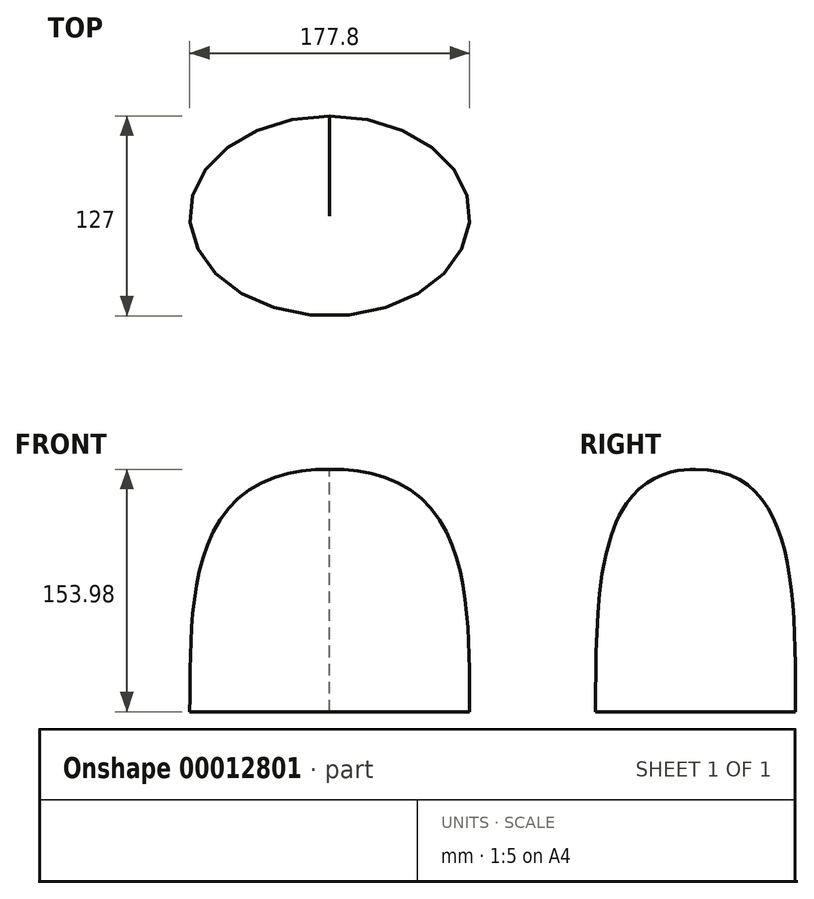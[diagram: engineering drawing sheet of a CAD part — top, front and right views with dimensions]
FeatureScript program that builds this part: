
annotation { "Feature Type Name" : "Feature", "Feature Type Description" : "" }
export const myFeature = defineFeature(function(context is Context, id is Id, definition is map)
    precondition{}
    {
        {
            var Q0;
            Q0=qCreatedBy(makeId("Top.planeOp"),FACE);
            var sketch = newSketch(context, id + "F0", { "sketchPlane" : qUnion([Q0])});
            skEllipse(sketch, "E0", {"center": v(0, 0) * mm, "majorRadius": 88.9 * mm, "minorRadius": 63.5 * mm, "majorAxis": v(-1, 0)});
            skSolve(sketch);
        }
        {
            var Q0;
            Q0=qCreatedBy(makeId("Front.planeOp"),FACE);
            var sketch = newSketch(context, id + "F1", { "sketchPlane" : qUnion([Q0])});
            skLineSegment(sketch, "E1", {"start": v(0, 0) * mm, "end": v(0, 153.98) * mm, "construction": true});
            skLineSegment(sketch, "E2", {"start": v(0, 153.98) * mm, "end": v(88.9, 0) * mm, "construction": true});
            skSolve(sketch);
        }
        {
            var Q0;
            Q0=makeQuery(id+"F0.imprint","IMPRINT",FACE,{"disambiguationData":[TD([[makeQuery(id+"F0.imprint","IMPRINT",EDGE,{"derivedFrom":sQuery(id+"F0.wireOp",EDGE,"E0")}),1.0]])]});
            var Q1;
            Q1=sQuery(id+"F1.wireOp",VERTEX,"E2.start");
            cPlane(context, id + "F2", {"entities" : qUnion([Q0, Q1]), "cplaneType" : CPlaneType.PLANE_POINT, "offset" : 25.4 * mm, "width" : 152.4 * mm, "height" : 152.4 * mm});
        }
        {
            var Q0;
            Q0=qCreatedBy(id+"F2.planeOp",FACE);
            var sketch = newSketch(context, id + "F3", { "sketchPlane" : qUnion([Q0])});
            skPoint(sketch, "E3.0", {"position": v(0, 0) * mm});
            skSolve(sketch);
        }
        {
            var Q0;
            Q0=makeQuery(id+"F0.imprint","IMPRINT",FACE,{"disambiguationData":[TD([[makeQuery(id+"F0.imprint","IMPRINT",EDGE,{"derivedFrom":sQuery(id+"F0.wireOp",EDGE,"E0")}),1.0]])]});
            var Q1;
            Q1=sQuery(id+"F3.wireOp",VERTEX,"E3.0");
            loft(context, id + "F4", {"endCondition" : LoftEndDerivativeType.TANGENT_TO_PROFILE, "endMagnitude" : 3, "sheetProfilesArray" : [{ "sheetProfileEntities" : qUnion([Q0]) }, { "sheetProfileEntities" : qUnion([Q1]) }]});
        }
    });
